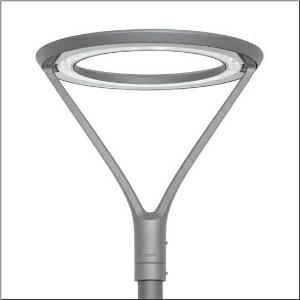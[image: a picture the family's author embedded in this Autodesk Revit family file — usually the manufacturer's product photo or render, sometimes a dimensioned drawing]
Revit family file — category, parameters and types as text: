
# Revit family: dl_r__20_led___pl1_2s_5xa512832s008_a952
name_source: partatom
category: Lighting Fixtures
units: mm (PartAtom-declared; Revit-internal decimal feet)

## family parameters
Cut with Voids When Loaded = No
Host = Face
Light Source = No
Part Type = Normal
Room Calculation Point = No
Round Connector Dimension = Use Diameter
Shared = No

## types (1)
- --- (1 x LED, 3030 lm, 33.7 W, 2200K)
    Apparent Load = 34 VA
    CIE Flux Codes = 34 78 98 100 100
    Color Rendering = 70
    Color Temperature = 2200K
    Default Elevation = 1800 mm
    Description = DL® 20 LED, mast luminaire, primary light control with reflector, highly specular, primary optical cover: cover, of toughened safety glass of clear glass with excellent transmission level, light distribution: PL1.2s, light emission: direct distribution, primary light characteristic: symmetric, installation type: post-top, LED, High Power LED, rated luminous flux: 3.040lm, luminous efficacy: 86lm/W, light colour: 722, colour temperature: 2200K, control gear: ECG Plus, control: flexible luminous flux parameterisation, time-dependent luminous flux control, constant luminous flux control, digital communication interface, power reduction, overheat protection, electronic power reduction, mains connection: 220..240V, 50/60Hz, connection cable pre-assembled, cable length: 5m, start of lifetime: 36W, end of lifetime: 36W, reduction: 17W, luminaire housing, upper part, of cast aluminium, powder-coated, Siteco® metallic grey (DB 702S), diameter: 690mm, height: 690mm, spigot size: 76mm (post-top), luminaire housing, of cast aluminium, powder-coated, Siteco® metallic grey (DB 702S), protection rating (complete): IP66, insulation class (complete): insulation class II (safety insulation), certification: CE, ENEC, VDE, impact resistance: IK08, permissible operating ambient temperature: -25..+35°C, standard-compliant lighting for roads and squares, packaging unit: 1 piece

Light Distribution: PL1.2s
    Height = 690 mm
    Lamp = 1 x LED
    Lamp Light Flux = 3030 lm
    Lamp Power = 33.7 W
    Lamp count = 1
    Length = 690 mm
    Luminous efficacy = 90 lm/W
    Manufacturer = Siteco
    ModVariant = No
    Model = 5XA512832S008
    Number of Poles = 1
    OnlyDefault = Yes
    Power Factor = 1
    Product Name = DL® 20 LED | PL1.2s
    Product group = mast luminaire | pylon top
    ProductGroupID = 6100
    Protection Class = Protection class II
    Protection Degree = IP 66
    RLX_Detail_Level = 1
    RlxData = <blob elided: 205465 chars, md5=ae730d4d>
    Socket = socket
    Standby Power = 0 W
    System Light Flux = 3030 lm
    System Power = 34 W
    Type Comments = factory setting: luminous flux: 100 % | dim-lin: 254 | 455 mA
    Type Image = l_1006001.jpg
    URL = http://relux.com
    VarID = @adj_118421
    Voltage = 0 V
    Weight = 0.00 kg
    Width = 0 mm  [stored 0 ft]

note: [stored X ft] marks values corroborated as IEEE doubles in the binary element streams (Revit-internal decimal feet)

## geometry (parser evidence)
native form markers: Blend x4, Sweep x11
no freeform markers — native parametric forms only
